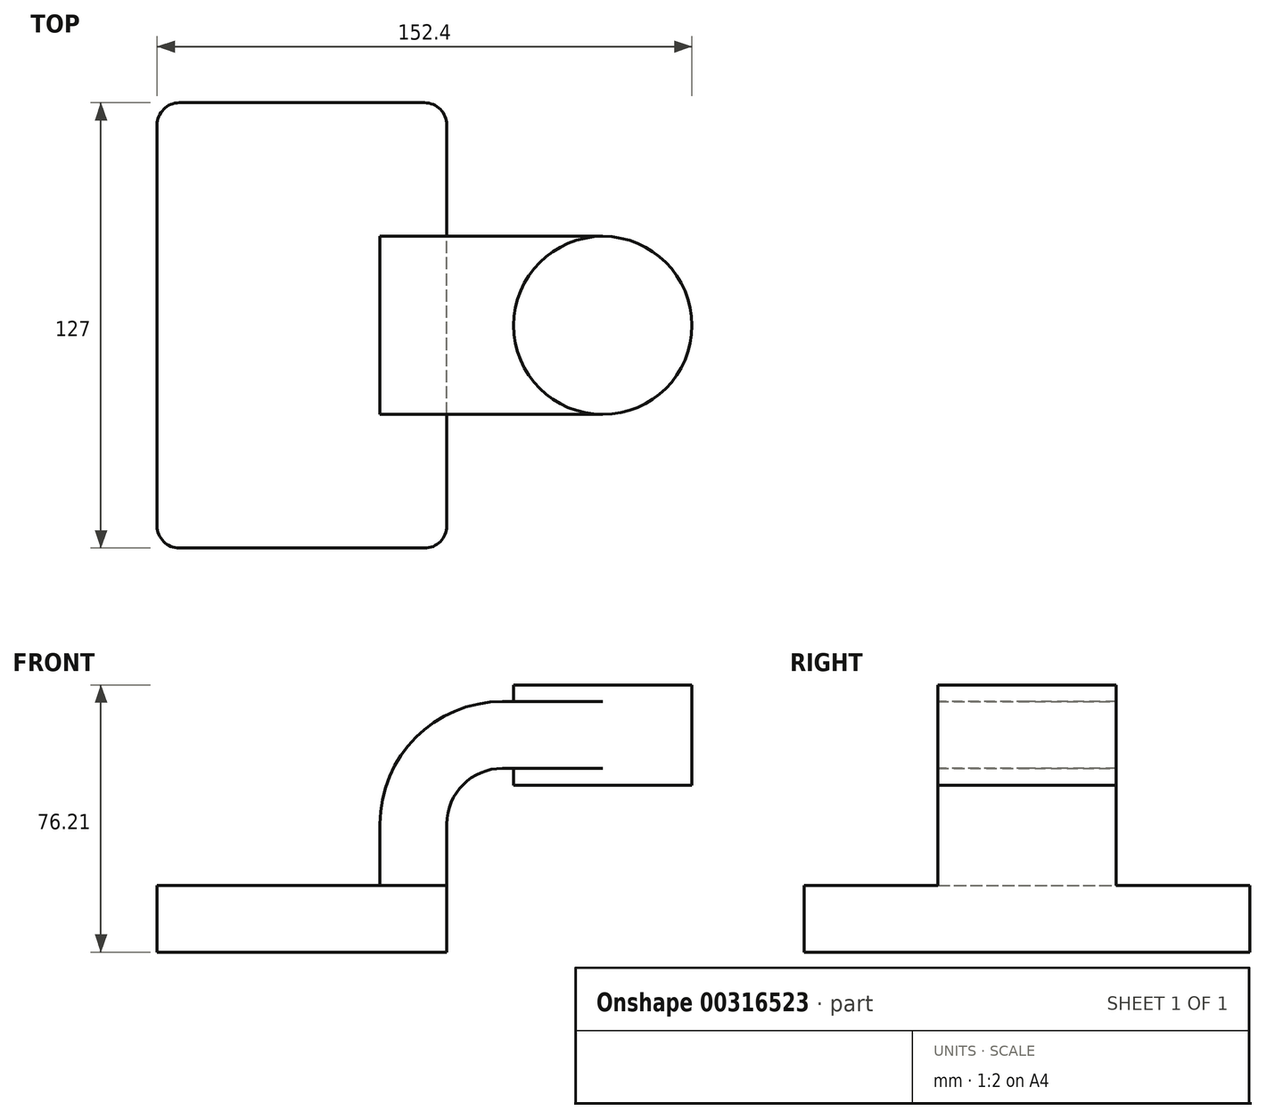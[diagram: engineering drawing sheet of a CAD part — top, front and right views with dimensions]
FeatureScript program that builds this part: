
annotation { "Feature Type Name" : "Feature", "Feature Type Description" : "" }
export const myFeature = defineFeature(function(context is Context, id is Id, definition is map)
    precondition{}
    {
        {
            var Q0;
            Q0=qCreatedBy(makeId("Front.planeOp"),FACE);
            var sketch = newSketch(context, id + "F0", { "sketchPlane" : qUnion([Q0])});
            skLineSegment(sketch, "E0.bottom", {"start": v(41.27, 9.53) * mm, "end": v(-41.28, 9.53) * mm});
            skLineSegment(sketch, "E0.top", {"start": v(41.28, -9.52) * mm, "end": v(-41.27, -9.52) * mm});
            skLineSegment(sketch, "E0.left", {"start": v(41.28, 9.53) * mm, "end": v(41.28, -9.52) * mm});
            skLineSegment(sketch, "E0.right", {"start": v(-41.28, 9.53) * mm, "end": v(-41.27, -9.52) * mm});
            skPoint(sketch, "E0.middle", {"position": v(0, 0) * mm});
            skLineSegment(sketch, "E1.bottom", {"start": v(111.12, 66.68) * mm, "end": v(60.32, 66.68) * mm});
            skLineSegment(sketch, "E1.top", {"start": v(111.12, 38.1) * mm, "end": v(60.32, 38.1) * mm});
            skLineSegment(sketch, "E1.left", {"start": v(111.12, 66.68) * mm, "end": v(111.12, 38.1) * mm});
            skLineSegment(sketch, "E1.right", {"start": v(60.32, 66.68) * mm, "end": v(60.32, 38.1) * mm});
            skPoint(sketch, "E1.middle", {"position": v(85.72, 52.39) * mm});
            skLineSegment(sketch, "E2", {"start": v(41.27, 9.53) * mm, "end": v(41.27, 27) * mm});
            skArc(sketch, "E3", {"start": v(41.27, 27) * mm, "mid": v(45.92, 38.23) * mm, "end": v(57.15, 42.88) * mm});
            skLineSegment(sketch, "E4", {"start": v(57.15, 42.88) * mm, "end": v(85.72, 42.88) * mm});
            skLineSegment(sketch, "E5.0", {"start": v(57.15, 61.93) * mm, "end": v(85.72, 61.93) * mm});
            skArc(sketch, "E5.1", {"start": v(22.22, 27) * mm, "mid": v(32.45, 51.7) * mm, "end": v(57.15, 61.93) * mm});
            skLineSegment(sketch, "E5.2", {"start": v(22.22, 9.53) * mm, "end": v(22.22, 27) * mm});
            skLineSegment(sketch, "E6", {"start": v(85.72, 38.1) * mm, "end": v(85.72, 66.68) * mm});
            skFitSpline(sketch, "E7", {"points": [v(-41.28, 9.53) * mm, v(57.15, 61.93) * mm], "startDerivative": vector(5.52, 98.12) * mm, "endDerivative": vector(95.67, -13.64) * mm});
            skSolve(sketch);
        }
        {
            var Q0;
            Q0=makeQuery(id+"F0.imprint","IMPRINT",FACE,{"disambiguationData":[TD([[makeQuery(id+"F0.imprint","IMPRINT",EDGE,{"derivedFrom":sQuery(id+"F0.wireOp",EDGE,"E0.top")}),-1.0]])]});
            extrude(context, id + "F1", {"entities" : qUnion([Q0]), "endBound" : BoundingType.SYMMETRIC, "depth" : 127 * mm});
        }
        {
            var Q0;
            {var subQ1=sQuery(id+"F0.wireOp",EDGE,"E2");Q0=makeQuery(id+"F0.imprint","IMPRINT",FACE,{"disambiguationData":[TD([[makeQuery(id+"F0.imprint","IMPRINT",EDGE,{"derivedFrom":subQ1}),1.0]])]});}
            var Q1;
            {var subQ0=sQuery(id+"F0.wireOp",EDGE,"E5.0");var subQ1=sQuery(id+"F0.wireOp",EDGE,"E1.right");var subQ2=makeQuery(id+"F0.imprint","INTERSECT",VERTEX,{"derivedFrom":[subQ1,subQ0]});Q1=makeQuery(id+"F0.imprint","IMPRINT",FACE,{"disambiguationData":[TD([[makeQuery(id+"F0.imprint","IMPRINT",EDGE,{"disambiguationData":[TD([[subQ2,-1.0]])],"derivedFrom":subQ1}),1.0]])]});}
            extrude(context, id + "F2", {"entities" : qUnion([Q0, Q1]), "operationType" : NewBodyOperationType.ADD, "endBound" : BoundingType.SYMMETRIC, "depth" : 50.8 * mm});
        }
        {
            var Q0;
            Q0=makeQuery(id+"F0.imprint","IMPRINT",FACE,{"disambiguationData":[TD([[makeQuery(id+"F0.imprint","IMPRINT",EDGE,{"derivedFrom":sQuery(id+"F0.wireOp",EDGE,"E5.1")}),1.0]])]});
            extrude(context, id + "F3", {"entities" : qUnion([Q0]), "operationType" : NewBodyOperationType.ADD, "endBound" : BoundingType.SYMMETRIC, "depth" : 15.88 * mm});
        }
        {
            var Q0;
            {var subQ4=sQuery(id+"F0.wireOp",EDGE,"E1.left");Q0=makeQuery(id+"F0.imprint","IMPRINT",FACE,{"disambiguationData":[TD([[makeQuery(id+"F0.imprint","IMPRINT",EDGE,{"derivedFrom":subQ4}),-1.0]])]});}
            var Q1;
            Q1=sQuery(id+"F0.wireOp",EDGE,"E6");
            revolve(context, id + "F4", {"operationType" : NewBodyOperationType.ADD, "entities" : qUnion([Q0]), "axis" : qUnion([Q1]), "revolveType" : RevolveType.FULL});
        }
        {
            var Q0;
            Q0=makeQuery(id+"F1.opExtrude","CAP_EDGE",EDGE,{"disambiguationData":[OSD([sQuery(id+"F0.wireOp",EDGE,"E0.right")])],"isStart":false});
            var Q1;
            Q1=makeQuery(id+"F1.opExtrude","CAP_EDGE",EDGE,{"disambiguationData":[OSD([sQuery(id+"F0.wireOp",EDGE,"E0.right")])],"isStart":true});
            var Q2;
            Q2=makeQuery(id+"F1.opExtrude","CAP_EDGE",EDGE,{"disambiguationData":[OSD([sQuery(id+"F0.wireOp",EDGE,"E0.left")])],"isStart":true});
            var Q3;
            Q3=makeQuery(id+"F1.opExtrude","CAP_EDGE",EDGE,{"disambiguationData":[OSD([sQuery(id+"F0.wireOp",EDGE,"E0.left")])],"isStart":false});
            fillet(context, id + "F5", {"entities" : qUnion([Q0, Q1, Q2, Q3]), "radius" : 6.35 * mm, "tangentPropagation" : true, "allowEdgeOverflow" : false});
        }
    });
